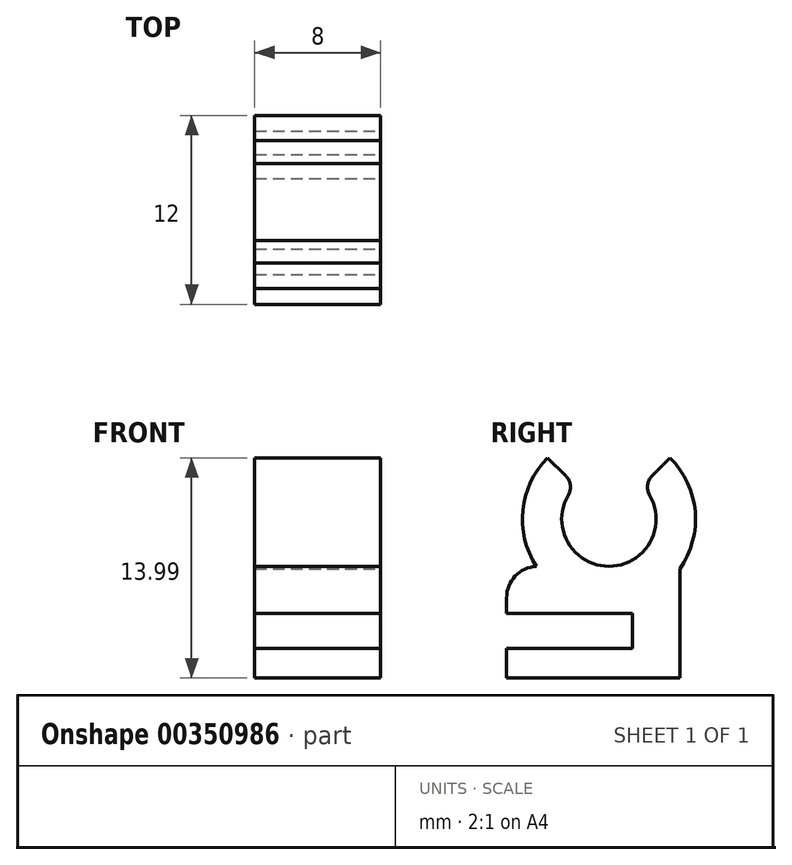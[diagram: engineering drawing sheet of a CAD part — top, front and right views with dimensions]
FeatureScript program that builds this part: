
annotation { "Feature Type Name" : "Feature", "Feature Type Description" : "" }
export const myFeature = defineFeature(function(context is Context, id is Id, definition is map)
    precondition{}
    {
        {
            var Q0;
            Q0=qCreatedBy(makeId("Front.planeOp"),FACE);
            var sketch = newSketch(context, id + "F0", { "sketchPlane" : qUnion([Q0])});
            skArc(sketch, "E0", {"start": v(-1.37, 3.76) * mm, "mid": v(-3.28, 2.3) * mm, "end": v(-4, 0) * mm});
            skArc(sketch, "E1", {"start": v(-1.03, 2.82) * mm, "mid": v(0, -3) * mm, "end": v(1.03, 2.82) * mm});
            skLineSegment(sketch, "E2", {"start": v(-1.03, 2.82) * mm, "end": v(-2.26, 6.2) * mm});
            skLineSegment(sketch, "E3", {"start": v(-2.26, 6.2) * mm, "end": v(-1.03, 2.82) * mm});
            skLineSegment(sketch, "E4", {"start": v(1.03, 2.82) * mm, "end": v(2.22, 6.11) * mm});
            skLineSegment(sketch, "E5.top", {"start": v(-4, -13) * mm, "end": v(4, -13) * mm});
            skLineSegment(sketch, "E5.left", {"start": v(-4, -8) * mm, "end": v(-4, -13) * mm});
            skLineSegment(sketch, "E5.right", {"start": v(4, -3) * mm, "end": v(4, -13) * mm});
            skLineSegment(sketch, "E6", {"start": v(-4, -8) * mm, "end": v(-4, 0) * mm});
            skLineSegment(sketch, "E7", {"start": v(4, 0) * mm, "end": v(4, -3) * mm});
            skArc(sketch, "E8.trimOffspring", {"start": v(4, 0) * mm, "mid": v(3.28, 2.3) * mm, "end": v(1.37, 3.76) * mm});
            skSolve(sketch);
        }
        {
            var Q0;
            Q0=qSketchRegion(id+"F0",true);
            extrude(context, id + "F1", {"entities" : qUnion([Q0]), "depth" : 4 * mm});
        }
        {
            var Q0;
            Q0=makeQuery(id+"F1.opExtrude","SWEPT_EDGE",EDGE,{"disambiguationData":[OSD([sQuery(id+"F0.wireOp",EDGE,"E0"),sQuery(id+"F0.wireOp",EDGE,"E3")])]});
            var Q1;
            Q1=makeQuery(id+"F1.opExtrude","SWEPT_EDGE",EDGE,{"disambiguationData":[OSD([sQuery(id+"F0.wireOp",EDGE,"E4"),sQuery(id+"F0.wireOp",EDGE,"E8.trimOffspring")])]});
            fillet(context, id + "F2", {"entities" : qUnion([Q0, Q1]), "radius" : 1 * mm, "tangentPropagation" : true, "allowEdgeOverflow" : false});
        }
        {
            var Q0;
            Q0=makeQuery(id+"F1.opExtrude","CAP_FACE",FACE,{"disambiguationData":[OSD([sQuery(id+"F0.wireOp",EDGE,"E0"),sQuery(id+"F0.wireOp",EDGE,"E1"),sQuery(id+"F0.wireOp",EDGE,"E3"),sQuery(id+"F0.wireOp",EDGE,"E4"),sQuery(id+"F0.wireOp",EDGE,"E5.top"),sQuery(id+"F0.wireOp",EDGE,"E5.left"),sQuery(id+"F0.wireOp",EDGE,"E5.right"),sQuery(id+"F0.wireOp",EDGE,"E6"),sQuery(id+"F0.wireOp",EDGE,"E7"),sQuery(id+"F0.wireOp",EDGE,"E8.trimOffspring")])],"isStart":false});
            var sketch = newSketch(context, id + "F3", { "sketchPlane" : qUnion([Q0])});
            skPoint(sketch, "E9.oppositeSnap0", {"position": v(0, -3) * mm});
            skLineSegment(sketch, "E9.bottom", {"start": v(4, -13) * mm, "end": v(-4, -13) * mm});
            skLineSegment(sketch, "E9.top", {"start": v(4, -3) * mm, "end": v(-4, -3) * mm});
            skLineSegment(sketch, "E9.left", {"start": v(4, -13) * mm, "end": v(4, -3) * mm});
            skLineSegment(sketch, "E9.right", {"start": v(-4, -13) * mm, "end": v(-4, -3) * mm});
            skSolve(sketch);
        }
        {
            var Q0;
            Q0=qSketchRegion(id+"F3",true);
            extrude(context, id + "F4", {"entities" : qUnion([Q0]), "operationType" : NewBodyOperationType.ADD, "depth" : 7 * mm});
        }
        {
            var Q0;
            Q0=makeQuery(id+"F4.boolean.opBoolean","MERGE",FACE,{"derivedFrom":[makeQuery(id+"F1.opExtrude","SWEPT_FACE",FACE,{"disambiguationData":[OSD([sQuery(id+"F0.wireOp",EDGE,"E5.right"),sQuery(id+"F0.wireOp",EDGE,"E7")])]}),makeQuery(id+"F4.opExtrude","SWEPT_FACE",FACE,{"disambiguationData":[OSD([sQuery(id+"F3.wireOp",EDGE,"E9.left")])]})]});
            var sketch = newSketch(context, id + "F5", { "sketchPlane" : qUnion([Q0])});
            skLineSegment(sketch, "E10.right", {"start": v(-3, -6) * mm, "end": v(-3, -8.2) * mm});
            skPoint(sketch, "E11.end.orphan", {"position": v(-11, -10.1) * mm});
            skPoint(sketch, "E12.end.orphan", {"position": v(-11, -3.1) * mm});
            skLineSegment(sketch, "E13.bottom", {"start": v(-3, -6) * mm, "end": v(-11, -6) * mm});
            skLineSegment(sketch, "E14", {"start": v(-3, -8.2) * mm, "end": v(-11, -8.2) * mm});
            skLineSegment(sketch, "E15", {"start": v(-11, -8.2) * mm, "end": v(-11, -6) * mm});
            skLineSegment(sketch, "E16.bottom", {"start": v(-11, -10.1) * mm, "end": v(0, -10.1) * mm});
            skLineSegment(sketch, "E16.top", {"start": v(-11, -13) * mm, "end": v(0, -13) * mm});
            skLineSegment(sketch, "E16.left", {"start": v(-11, -10.1) * mm, "end": v(-11, -13) * mm});
            skLineSegment(sketch, "E16.right", {"start": v(0, -10.1) * mm, "end": v(0, -13) * mm});
            skSolve(sketch);
        }
        {
            var Q0;
            Q0 = qSketchRegion(id + "F5", true);
            extrude(context, id + "F6", {"entities" : qUnion([Q0]), "operationType" : NewBodyOperationType.REMOVE, "oppositeDirection" : true, "depth" : 25 * mm});
        }
        {
            var Q0;
            Q0=makeQuery(id+"F6.boolean.opBoolean","COPY",EDGE,{"derivedFrom":makeQuery(id+"F6.opExtrude","SWEPT_EDGE",EDGE,{"disambiguationData":[OSD([sQuery(id+"F3.wireOp",EDGE,"E9.left"),sQuery(id+"F5.wireOp",EDGE,"E13.bottom"),sQuery(id+"F5.wireOp",EDGE,"E15")])]})});
            var Q1;
            Q1=makeQuery(id+"F6.boolean.opBoolean","COPY",EDGE,{"derivedFrom":makeQuery(id+"F6.opExtrude","SWEPT_EDGE",EDGE,{"disambiguationData":[OSD([sQuery(id+"F3.wireOp",EDGE,"E9.left"),sQuery(id+"F5.wireOp",EDGE,"E14"),sQuery(id+"F5.wireOp",EDGE,"E15")])]})});
            var Q2;
            Q2=makeQuery(id+"F4.opExtrude","CAP_EDGE",EDGE,{"disambiguationData":[OSD([sQuery(id+"F3.wireOp",EDGE,"E9.top")])],"isStart":false});
            var Q3;
            Q3=makeQuery(id+"F6.boolean.opBoolean","COPY",EDGE,{"derivedFrom":makeQuery(id+"F6.opExtrude","SWEPT_EDGE",EDGE,{"disambiguationData":[OSD([sQuery(id+"F0.wireOp",EDGE,"E5.right"),sQuery(id+"F0.wireOp",EDGE,"E7"),sQuery(id+"F5.wireOp",EDGE,"E16.bottom"),sQuery(id+"F5.wireOp",EDGE,"E16.right")])]})});
            fillet(context, id + "F7", {"entities" : qUnion([Q0, Q1, Q2, Q3]), "radius" : 2 * mm, "tangentPropagation" : true, "allowEdgeOverflow" : false});
        }
        {
            var Q0;
            {var subQ0=sQuery(id+"F0.wireOp",EDGE,"E8.trimOffspring");var subQ1=sQuery(id+"F0.wireOp",EDGE,"E7");var subQ2=sQuery(id+"F0.wireOp",EDGE,"E5.right");var subQ3=sQuery(id+"F0.wireOp",EDGE,"E1");var subQ4=sQuery(id+"F0.wireOp",EDGE,"E4");var subQ5=makeQuery(id+"F1.opExtrude","CAP_FACE",FACE,{"disambiguationData":[OSD([sQuery(id+"F0.wireOp",EDGE,"E0"),subQ3,sQuery(id+"F0.wireOp",EDGE,"E3"),subQ4,sQuery(id+"F0.wireOp",EDGE,"E5.top"),sQuery(id+"F0.wireOp",EDGE,"E5.left"),subQ2,sQuery(id+"F0.wireOp",EDGE,"E6"),subQ1,subQ0])],"isStart":false});Q0=makeQuery(id+"F4.boolean.opBoolean","SPLIT",FACE,{"disambiguationData":[TD([makeQuery(id+"F1.opExtrude","SWEPT_FACE",FACE,{"disambiguationData":[OSD([subQ0])]})])],"derivedFrom":subQ5});}
            var sketch = newSketch(context, id + "F8", { "sketchPlane" : qUnion([Q0])});
            skLineSegment(sketch, "E17.bottom", {"start": v(4, -3) * mm, "end": v(-6.98, -3) * mm});
            skLineSegment(sketch, "E17.top", {"start": v(4, 4.87) * mm, "end": v(-6.98, 4.87) * mm});
            skLineSegment(sketch, "E17.left", {"start": v(4, -3) * mm, "end": v(4, 4.87) * mm});
            skLineSegment(sketch, "E17.right", {"start": v(-6.98, -3) * mm, "end": v(-6.98, 4.87) * mm});
            skSolve(sketch);
        }
        {
            var Q0;
            Q0 = qSketchRegion(id + "F8", true);
            extrude(context, id + "F9", {"entities" : qUnion([Q0]), "operationType" : NewBodyOperationType.REMOVE, "oppositeDirection" : true, "depth" : 25 * mm});
        }
        {
            var Q0;
            Q0=makeQuery(id+"F4.boolean.opBoolean","MERGE",FACE,{"derivedFrom":[makeQuery(id+"F1.opExtrude","SWEPT_FACE",FACE,{"disambiguationData":[OSD([sQuery(id+"F0.wireOp",EDGE,"E5.right"),sQuery(id+"F0.wireOp",EDGE,"E7")])]}),makeQuery(id+"F4.opExtrude","SWEPT_FACE",FACE,{"disambiguationData":[OSD([sQuery(id+"F3.wireOp",EDGE,"E9.left")])]})]});
            var sketch = newSketch(context, id + "F10", { "sketchPlane" : qUnion([Q0])});
            skLineSegment(sketch, "E18.bottom", {"start": v(0, -3) * mm, "end": v(-9.1, -3) * mm});
            skArc(sketch, "E19", {"start": v(-6.62, 2.12) * mm, "mid": v(-4.5, -3) * mm, "end": v(-2.38, 2.12) * mm});
            skPoint(sketch, "E19.centerSnap0", {"position": v(-4.5, -3) * mm});
            skArc(sketch, "E20", {"start": v(-8.39, 3.89) * mm, "mid": v(-4.5, -5.5) * mm, "end": v(-0.61, 3.89) * mm});
            skLineSegment(sketch, "E21", {"start": v(-6.62, 2.12) * mm, "end": v(-8.39, 3.89) * mm});
            skLineSegment(sketch, "E22", {"start": v(-2.38, 2.12) * mm, "end": v(-0.61, 3.89) * mm});
            skPoint(sketch, "E23.orphan", {"position": v(0, 4.5) * mm});
            skSolve(sketch);
        }
        {
            var Q0;
            Q0 = qSketchRegion(id + "F10", true);
            var Q1;
            Q1=makeQuery(id+"F4.boolean.opBoolean","MERGE",FACE,{"derivedFrom":[makeQuery(id+"F1.opExtrude","SWEPT_FACE",FACE,{"disambiguationData":[OSD([sQuery(id+"F0.wireOp",EDGE,"E5.left"),sQuery(id+"F0.wireOp",EDGE,"E6")])]}),makeQuery(id+"F4.opExtrude","SWEPT_FACE",FACE,{"disambiguationData":[OSD([sQuery(id+"F3.wireOp",EDGE,"E9.right")])]})]});
            extrude(context, id + "F11", {"entities" : qUnion([Q0]), "operationType" : NewBodyOperationType.ADD, "endBound" : BoundingType.UP_TO_SURFACE, "oppositeDirection" : true, "endBoundEntityFace" : qUnion([Q1]), "depth" : 25 * mm});
        }
        {
            var Q0;
            Q0=makeQuery(id+"F11.opExtrude","SWEPT_EDGE",EDGE,{"disambiguationData":[OSD([sQuery(id+"F10.wireOp",EDGE,"E19"),sQuery(id+"F10.wireOp",EDGE,"E22")])]});
            var Q1;
            Q1=makeQuery(id+"F11.opExtrude","SWEPT_EDGE",EDGE,{"disambiguationData":[OSD([sQuery(id+"F10.wireOp",EDGE,"E19"),sQuery(id+"F10.wireOp",EDGE,"E21")])]});
            fillet(context, id + "F12", {"entities" : qUnion([Q0, Q1]), "radius" : 1 * mm, "tangentPropagation" : true, "allowEdgeOverflow" : false});
        }
    });
